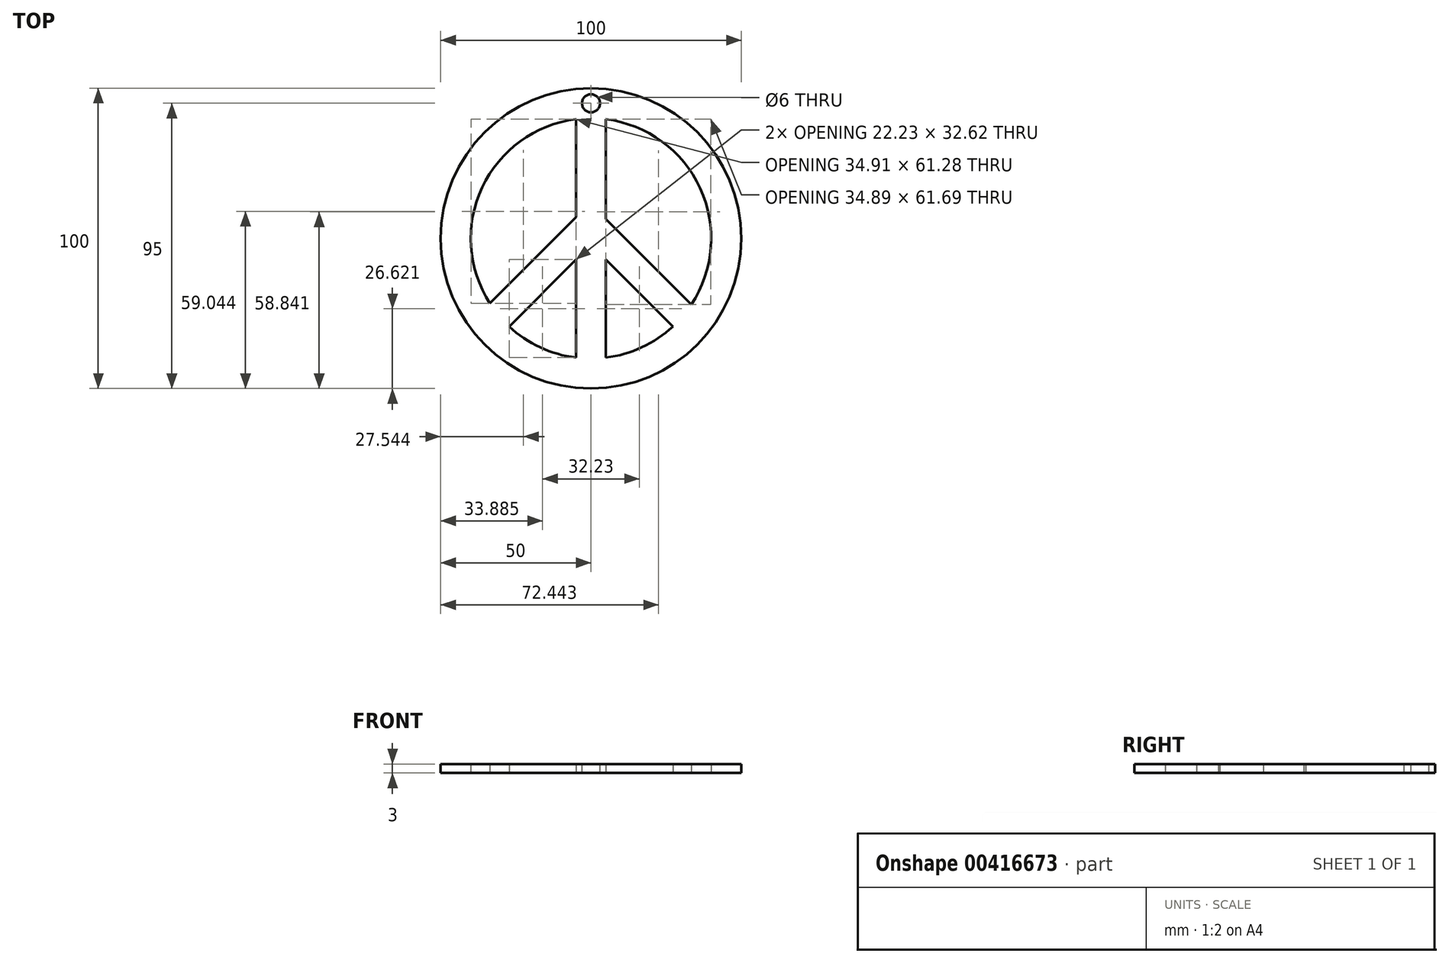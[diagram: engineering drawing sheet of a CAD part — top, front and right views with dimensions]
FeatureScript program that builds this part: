
annotation { "Feature Type Name" : "Feature", "Feature Type Description" : "" }
export const myFeature = defineFeature(function(context is Context, id is Id, definition is map)
    precondition{}
    {
        {
            var Q0;
            Q0=qCreatedBy(makeId("Top.planeOp"),FACE);
            var sketch = newSketch(context, id + "F0", { "sketchPlane" : qUnion([Q0])});
            skCircle(sketch, "E0", {"center": v(0, 0) * mm, "radius": 50 * mm});
            skArc(sketch, "E1", {"start": v(-5, 39.69) * mm, "mid": v(-36.23, 16.95) * mm, "end": v(-33.67, -21.6) * mm});
            skLineSegment(sketch, "E2", {"start": v(-5, 7.07) * mm, "end": v(-5, 39.69) * mm});
            skLineSegment(sketch, "E3", {"start": v(5, 6.4) * mm, "end": v(5, 39.69) * mm});
            skLineSegment(sketch, "E4", {"start": v(-5, -7.07) * mm, "end": v(-5, -39.69) * mm});
            skLineSegment(sketch, "E5", {"start": v(5, -7.07) * mm, "end": v(5, -39.69) * mm});
            skLineSegment(sketch, "E6", {"start": v(21.88, -10.48) * mm, "end": v(11.4, 0) * mm});
            skLineSegment(sketch, "E7", {"start": v(21.88, -10.48) * mm, "end": v(33.4, -22) * mm});
            skLineSegment(sketch, "E8", {"start": v(15.14, -17.21) * mm, "end": v(5, -7.07) * mm});
            skLineSegment(sketch, "E9", {"start": v(15.14, -17.21) * mm, "end": v(27.23, -29.3) * mm});
            skLineSegment(sketch, "E10", {"start": v(21.88, -10.48) * mm, "end": v(5, 6.4) * mm});
            skLineSegment(sketch, "E11", {"start": v(-23.87, -11.8) * mm, "end": v(-5, 7.07) * mm});
            skLineSegment(sketch, "E12", {"start": v(-23.87, -11.8) * mm, "end": v(-33.67, -21.6) * mm});
            skLineSegment(sketch, "E13", {"start": v(-16.8, -18.87) * mm, "end": v(-5, -7.07) * mm});
            skLineSegment(sketch, "E14", {"start": v(-16.8, -18.87) * mm, "end": v(-27.23, -29.3) * mm});
            skArc(sketch, "E15.trimOffspring", {"start": v(5, -39.69) * mm, "mid": v(16.93, -36.24) * mm, "end": v(27.23, -29.3) * mm});
            skArc(sketch, "E16.trimOffspring", {"start": v(33.4, -22) * mm, "mid": v(36.33, 16.73) * mm, "end": v(5, 39.69) * mm});
            skArc(sketch, "E17.trimOffspring", {"start": v(-27.23, -29.3) * mm, "mid": v(-16.93, -36.24) * mm, "end": v(-5, -39.69) * mm});
            skSolve(sketch);
        }
        {
            var Q0;
            Q0 = qSketchRegion(id + "F0", true);
            extrude(context, id + "F1", {"entities" : qUnion([Q0]), "depth" : 3 * mm});
        }
        {
            var Q0;
            Q0 = qSketchRegion(id + "F0", true);
            extrude(context, id + "F2", {"entities" : qUnion([Q0]), "operationType" : NewBodyOperationType.ADD, "depth" : 3 * mm});
        }
        {
            var Q0;
            Q0=makeQuery(id+"F1.opExtrude","CAP_FACE",FACE,{"disambiguationData":[OSD([sQuery(id+"F0.wireOp",EDGE,"E0"),sQuery(id+"F0.wireOp",EDGE,"E1"),sQuery(id+"F0.wireOp",EDGE,"E2"),sQuery(id+"F0.wireOp",EDGE,"E3"),sQuery(id+"F0.wireOp",EDGE,"E4"),sQuery(id+"F0.wireOp",EDGE,"E5"),sQuery(id+"F0.wireOp",EDGE,"E7"),sQuery(id+"F0.wireOp",EDGE,"E8"),sQuery(id+"F0.wireOp",EDGE,"E9"),sQuery(id+"F0.wireOp",EDGE,"E10"),sQuery(id+"F0.wireOp",EDGE,"E11"),sQuery(id+"F0.wireOp",EDGE,"E12"),sQuery(id+"F0.wireOp",EDGE,"E13"),sQuery(id+"F0.wireOp",EDGE,"E14"),sQuery(id+"F0.wireOp",EDGE,"E15.trimOffspring"),sQuery(id+"F0.wireOp",EDGE,"E16.trimOffspring"),sQuery(id+"F0.wireOp",EDGE,"E17.trimOffspring")])],"isStart":false});
            var sketch = newSketch(context, id + "F3", { "sketchPlane" : qUnion([Q0])});
            skLineSegment(sketch, "E18", {"start": v(0, 0) * mm, "end": v(0, 45) * mm});
            skCircle(sketch, "E19", {"center": v(0, 45) * mm, "radius": 3 * mm});
            skSolve(sketch);
        }
        {
            var Q0;
            Q0=makeQuery(id+"F3.imprint","IMPRINT",FACE,{"disambiguationData":[TD([[makeQuery(id+"F3.imprint","IMPRINT",EDGE,{"derivedFrom":sQuery(id+"F3.wireOp",EDGE,"E19")}),1.0]])]});
            extrude(context, id + "F4", {"entities" : qUnion([Q0]), "operationType" : NewBodyOperationType.REMOVE, "oppositeDirection" : true, "depth" : 25 * mm});
        }
    });
